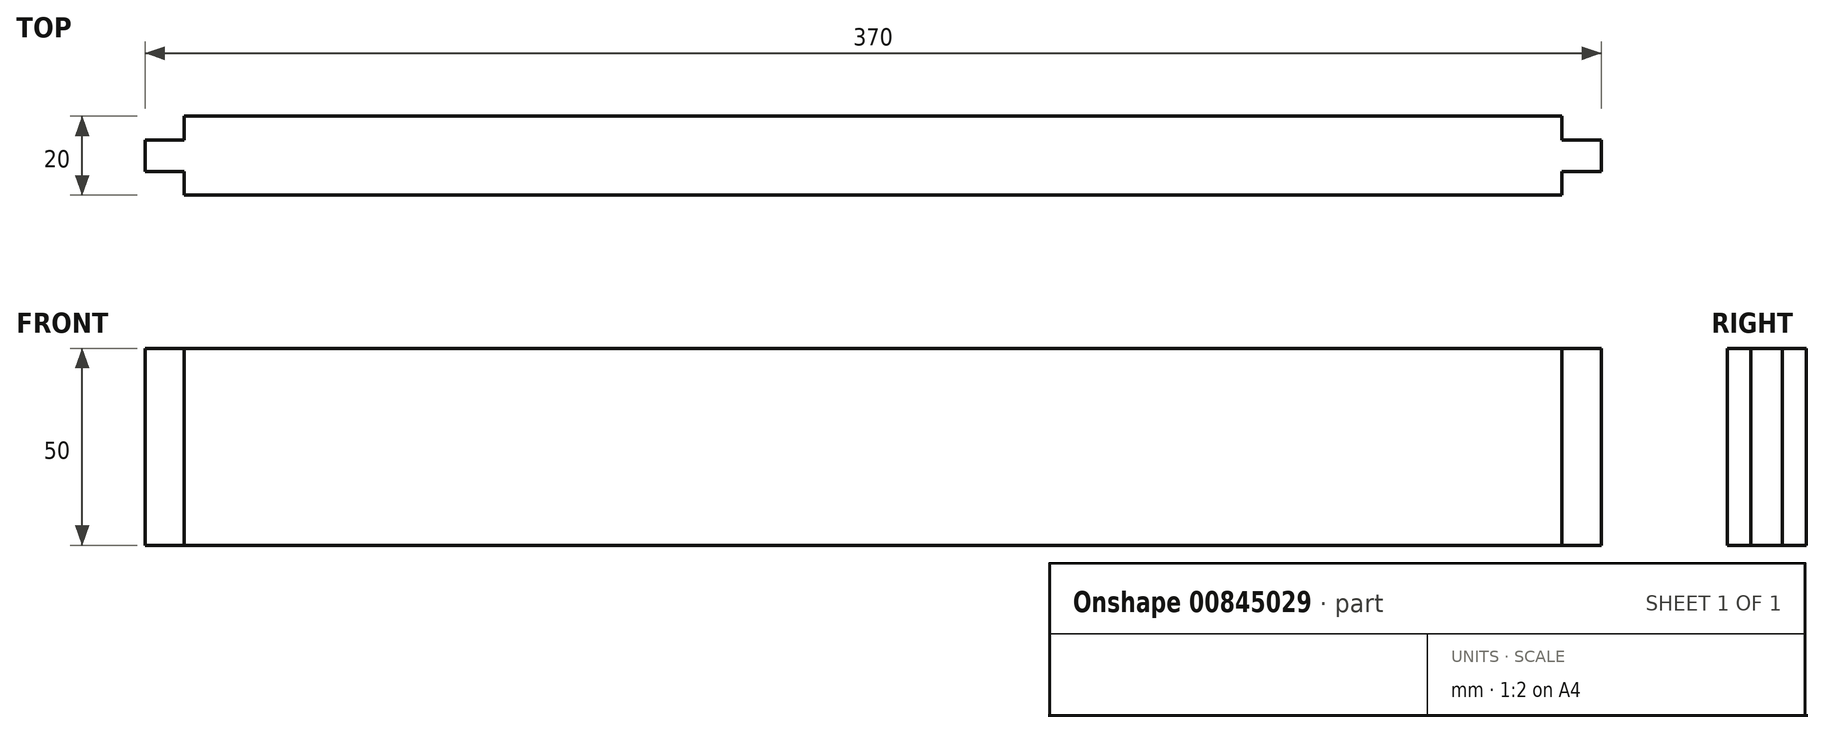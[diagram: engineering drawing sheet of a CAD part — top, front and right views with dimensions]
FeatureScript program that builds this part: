
annotation { "Feature Type Name" : "Feature", "Feature Type Description" : "" }
export const myFeature = defineFeature(function(context is Context, id is Id, definition is map)
    precondition{}
    {
        {
            var Q0;
            Q0=qCreatedBy(makeId("Front.planeOp"),FACE);
            var sketch = newSketch(context, id + "F0", { "sketchPlane" : qUnion([Q0])});
            skLineSegment(sketch, "E0.bottom", {"start": v(-175, 25) * mm, "end": v(175, 25) * mm});
            skLineSegment(sketch, "E0.top", {"start": v(-175, -25) * mm, "end": v(175, -25) * mm});
            skLineSegment(sketch, "E0.left", {"start": v(-175, 25) * mm, "end": v(-175, -25) * mm});
            skLineSegment(sketch, "E0.right", {"start": v(175, 25) * mm, "end": v(175, -25) * mm});
            skPoint(sketch, "E0.middle", {"position": v(0, 0) * mm});
            skSolve(sketch);
        }
        {
            var Q0;
            Q0=makeQuery(id+"F0.imprint","IMPRINT",FACE,{"disambiguationData":[TD([[makeQuery(id+"F0.imprint","IMPRINT",EDGE,{"derivedFrom":sQuery(id+"F0.wireOp",EDGE,"E0.bottom")}),-1.0]])]});
            extrude(context, id + "F1", {"entities" : qUnion([Q0]), "depth" : 20 * mm, "offsetDistance" : 25 * mm});
        }
        {
            var Q0;
            Q0=makeQuery(id+"F1.opExtrude","SWEPT_FACE",FACE,{"disambiguationData":[OSD([sQuery(id+"F0.wireOp",EDGE,"E0.left")])]});
            var sketch = newSketch(context, id + "F2", { "sketchPlane" : qUnion([Q0])});
            skLineSegment(sketch, "E1.bottom", {"start": v(6, 25) * mm, "end": v(14, 25) * mm});
            skLineSegment(sketch, "E1.top", {"start": v(6, -25) * mm, "end": v(14, -25) * mm});
            skLineSegment(sketch, "E1.left", {"start": v(6, 25) * mm, "end": v(6, -25) * mm});
            skLineSegment(sketch, "E1.right", {"start": v(14, 25) * mm, "end": v(14, -25) * mm});
            skPoint(sketch, "E1.middle", {"position": v(10, 0) * mm});
            skSolve(sketch);
        }
        {
            var Q0;
            Q0=makeQuery(id+"F2.imprint","IMPRINT",FACE,{"disambiguationData":[TD([[makeQuery(id+"F2.imprint","IMPRINT",EDGE,{"derivedFrom":sQuery(id+"F2.wireOp",EDGE,"E1.bottom")}),1.0]])]});
            extrude(context, id + "F3", {"entities" : qUnion([Q0]), "operationType" : NewBodyOperationType.ADD, "depth" : 10 * mm, "offsetDistance" : 25 * mm});
        }
        {
            var Q0;
            Q0=makeQuery(id+"F1.opExtrude","SWEPT_FACE",FACE,{"disambiguationData":[OSD([sQuery(id+"F0.wireOp",EDGE,"E0.right")])]});
            var sketch = newSketch(context, id + "F4", { "sketchPlane" : qUnion([Q0])});
            skLineSegment(sketch, "E2.bottom", {"start": v(-14, 25) * mm, "end": v(-6, 25) * mm});
            skLineSegment(sketch, "E2.top", {"start": v(-14, -25) * mm, "end": v(-6, -25) * mm});
            skLineSegment(sketch, "E2.left", {"start": v(-14, 25) * mm, "end": v(-14, -25) * mm});
            skLineSegment(sketch, "E2.right", {"start": v(-6, 25) * mm, "end": v(-6, -25) * mm});
            skPoint(sketch, "E2.middle", {"position": v(-10, 0) * mm});
            skSolve(sketch);
        }
        {
            var Q0;
            Q0=makeQuery(id+"F4.imprint","IMPRINT",FACE,{"disambiguationData":[TD([[makeQuery(id+"F4.imprint","IMPRINT",EDGE,{"derivedFrom":sQuery(id+"F4.wireOp",EDGE,"E2.bottom")}),-1.0]])]});
            extrude(context, id + "F5", {"entities" : qUnion([Q0]), "operationType" : NewBodyOperationType.ADD, "depth" : 10 * mm, "offsetDistance" : 25 * mm});
        }
    });
